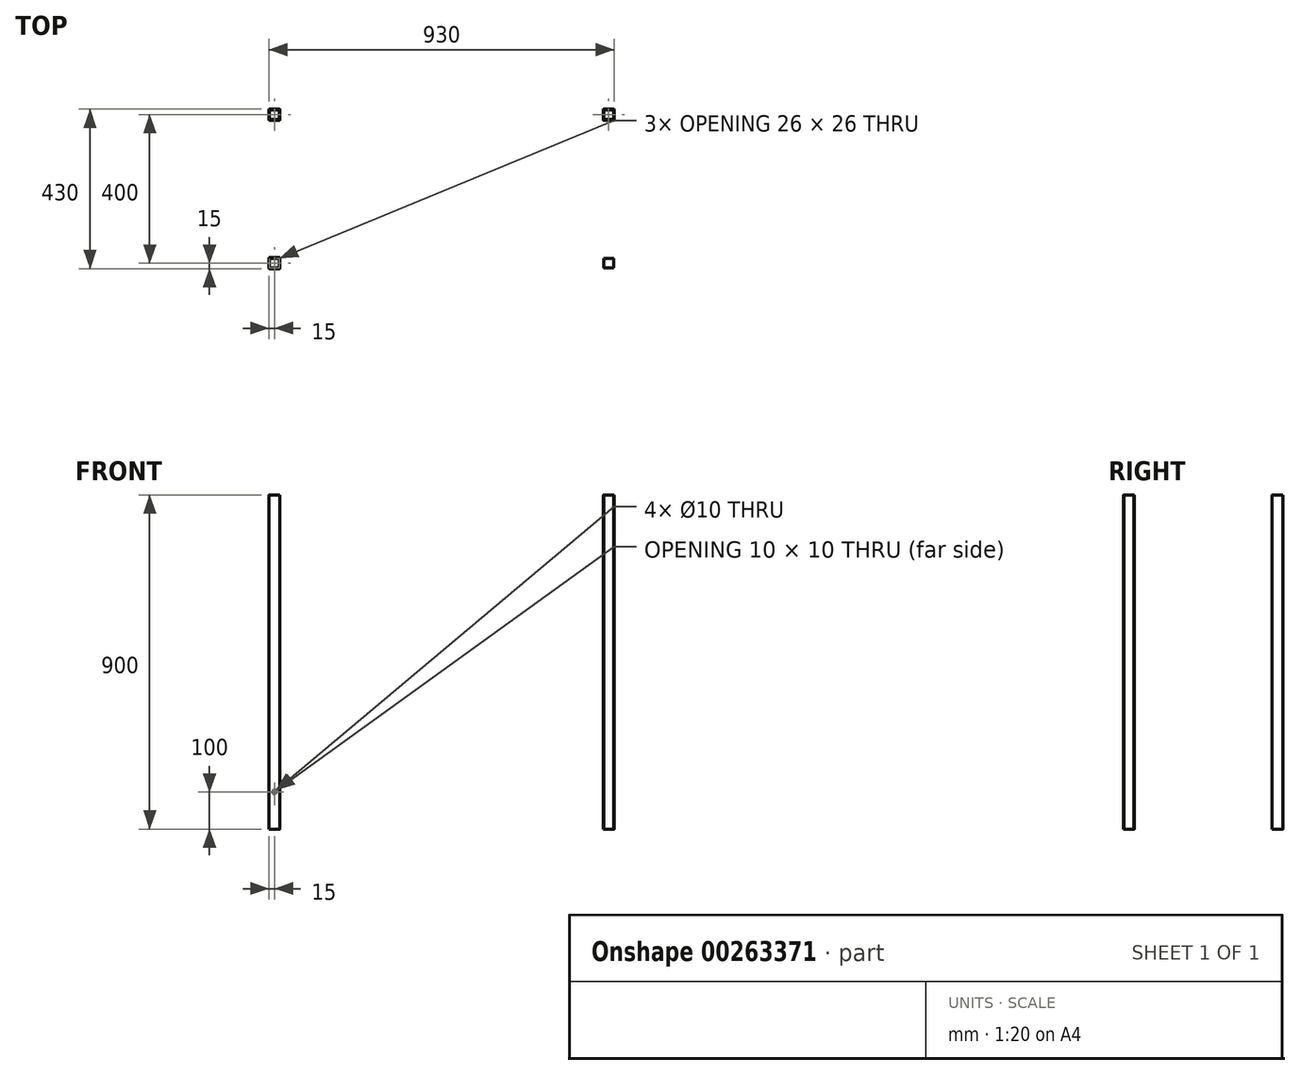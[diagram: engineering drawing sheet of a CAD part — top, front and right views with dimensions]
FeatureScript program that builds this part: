
annotation { "Feature Type Name" : "Feature", "Feature Type Description" : "" }
export const myFeature = defineFeature(function(context is Context, id is Id, definition is map)
    precondition{}
    {
        {
            var Q0;
            Q0=qCreatedBy(makeId("Top.planeOp"),FACE);
            var sketch = newSketch(context, id + "F0", { "sketchPlane" : qUnion([Q0])});
            skLineSegment(sketch, "E0.bottom", {"start": v(1, 0) * mm, "end": v(29, 0) * mm});
            skLineSegment(sketch, "E0.top", {"start": v(1, 30) * mm, "end": v(29, 30) * mm});
            skLineSegment(sketch, "E0.left", {"start": v(0, 1) * mm, "end": v(0, 29) * mm});
            skLineSegment(sketch, "E0.right", {"start": v(30, 1) * mm, "end": v(30, 29) * mm});
            skLineSegment(sketch, "E1.bottom", {"start": v(27, 28) * mm, "end": v(3, 28) * mm});
            skLineSegment(sketch, "E1.top", {"start": v(28, 2) * mm, "end": v(3, 2) * mm});
            skLineSegment(sketch, "E1.left", {"start": v(28, 27) * mm, "end": v(28, 2) * mm});
            skLineSegment(sketch, "E1.right", {"start": v(2, 27) * mm, "end": v(2, 3) * mm});
            skPoint(sketch, "E1.middle", {"position": v(15, 15) * mm});
            skLineSegment(sketch, "E2", {"start": v(15, 15) * mm, "end": v(15, 30) * mm, "construction": true});
            skLineSegment(sketch, "E3", {"start": v(15, 15) * mm, "end": v(0, 15) * mm, "construction": true});
            skPoint(sketch, "E4.visualSharp", {"position": v(0, 30) * mm});
            skArc(sketch, "E4.filletArc", {"start": v(1, 30) * mm, "mid": v(0.3, 29.7) * mm, "end": v(0, 29) * mm});
            skPoint(sketch, "E5.visualSharp", {"position": v(30, 30) * mm});
            skArc(sketch, "E5.filletArc", {"start": v(30, 29) * mm, "mid": v(29.7, 29.7) * mm, "end": v(29, 30) * mm});
            skPoint(sketch, "E6.visualSharp", {"position": v(30, 0) * mm});
            skArc(sketch, "E6.filletArc", {"start": v(29, 0) * mm, "mid": v(29.7, 0.3) * mm, "end": v(30, 1) * mm});
            skPoint(sketch, "E7.visualSharp", {"position": v(0, 0) * mm});
            skArc(sketch, "E7.filletArc", {"start": v(0, 1) * mm, "mid": v(0.3, 0.3) * mm, "end": v(1, 0) * mm});
            skPoint(sketch, "E8.visualSharp", {"position": v(2, 2) * mm});
            skArc(sketch, "E8.filletArc", {"start": v(2, 3) * mm, "mid": v(2.3, 2.3) * mm, "end": v(3, 2) * mm});
            skPoint(sketch, "E9.visualSharp", {"position": v(2, 28) * mm});
            skArc(sketch, "E9.filletArc", {"start": v(3, 28) * mm, "mid": v(2.3, 27.7) * mm, "end": v(2, 27) * mm});
            skPoint(sketch, "E10.visualSharp", {"position": v(28, 28) * mm});
            skArc(sketch, "E10.filletArc", {"start": v(28, 27) * mm, "mid": v(27.7, 27.7) * mm, "end": v(27, 28) * mm});
            skLineSegment(sketch, "E11.0.1.0", {"start": v(30, 401) * mm, "end": v(30, 429) * mm});
            skPoint(sketch, "E11.0.1.1", {"position": v(30, 430) * mm});
            skPoint(sketch, "E11.0.1.2", {"position": v(30, 400) * mm});
            skPoint(sketch, "E11.0.1.3", {"position": v(28, 428) * mm});
            skLineSegment(sketch, "E11.0.1.4", {"start": v(1, 400) * mm, "end": v(29, 400) * mm});
            skLineSegment(sketch, "E11.0.1.5", {"start": v(1, 430) * mm, "end": v(29, 430) * mm});
            skPoint(sketch, "E11.0.1.6", {"position": v(2, 428) * mm});
            skLineSegment(sketch, "E11.0.1.7", {"start": v(0, 401) * mm, "end": v(0, 429) * mm});
            skPoint(sketch, "E11.0.1.8", {"position": v(15, 415) * mm});
            skLineSegment(sketch, "E11.0.1.9", {"start": v(27, 428) * mm, "end": v(3, 428) * mm});
            skLineSegment(sketch, "E11.0.1.10", {"start": v(28, 427) * mm, "end": v(28, 402) * mm});
            skLineSegment(sketch, "E11.0.1.11", {"start": v(15, 415) * mm, "end": v(15, 430) * mm, "construction": true});
            skLineSegment(sketch, "E11.0.1.12", {"start": v(15, 415) * mm, "end": v(0, 415) * mm, "construction": true});
            skLineSegment(sketch, "E11.0.1.13", {"start": v(2, 427) * mm, "end": v(2, 403) * mm});
            skPoint(sketch, "E11.0.1.14", {"position": v(0, 400) * mm});
            skLineSegment(sketch, "E11.0.1.15", {"start": v(28, 402) * mm, "end": v(3, 402) * mm});
            skPoint(sketch, "E11.0.1.16", {"position": v(2, 402) * mm});
            skPoint(sketch, "E11.0.1.17", {"position": v(0, 430) * mm});
            skArc(sketch, "E11.0.1.18", {"start": v(1, 430) * mm, "mid": v(0.3, 429.7) * mm, "end": v(0, 429) * mm});
            skArc(sketch, "E11.0.1.19", {"start": v(30, 429) * mm, "mid": v(29.7, 429.7) * mm, "end": v(29, 430) * mm});
            skArc(sketch, "E11.0.1.20", {"start": v(28, 427) * mm, "mid": v(27.7, 427.7) * mm, "end": v(27, 428) * mm});
            skArc(sketch, "E11.0.1.21", {"start": v(0, 401) * mm, "mid": v(0.3, 400.3) * mm, "end": v(1, 400) * mm});
            skArc(sketch, "E11.0.1.22", {"start": v(2, 403) * mm, "mid": v(2.3, 402.3) * mm, "end": v(3, 402) * mm});
            skArc(sketch, "E11.0.1.23", {"start": v(3, 428) * mm, "mid": v(2.3, 427.7) * mm, "end": v(2, 427) * mm});
            skArc(sketch, "E11.0.1.24", {"start": v(29, 400) * mm, "mid": v(29.7, 400.3) * mm, "end": v(30, 401) * mm});
            skLineSegment(sketch, "E11.1.0.0", {"start": v(930, 1) * mm, "end": v(930, 29) * mm});
            skPoint(sketch, "E11.1.0.1", {"position": v(930, 30) * mm});
            skPoint(sketch, "E11.1.0.2", {"position": v(930, 0) * mm});
            skPoint(sketch, "E11.1.0.3", {"position": v(928, 28) * mm});
            skLineSegment(sketch, "E11.1.0.4", {"start": v(901, 0) * mm, "end": v(929, 0) * mm});
            skLineSegment(sketch, "E11.1.0.5", {"start": v(901, 30) * mm, "end": v(929, 30) * mm});
            skPoint(sketch, "E11.1.0.6", {"position": v(902, 28) * mm});
            skLineSegment(sketch, "E11.1.0.7", {"start": v(900, 1) * mm, "end": v(900, 29) * mm});
            skPoint(sketch, "E11.1.0.8", {"position": v(915, 15) * mm});
            skLineSegment(sketch, "E11.1.0.9", {"start": v(927, 28) * mm, "end": v(903, 28) * mm});
            skLineSegment(sketch, "E11.1.0.10", {"start": v(928, 27) * mm, "end": v(928, 2) * mm});
            skLineSegment(sketch, "E11.1.0.11", {"start": v(915, 15) * mm, "end": v(915, 30) * mm, "construction": true});
            skLineSegment(sketch, "E11.1.0.12", {"start": v(915, 15) * mm, "end": v(900, 15) * mm, "construction": true});
            skLineSegment(sketch, "E11.1.0.13", {"start": v(902, 27) * mm, "end": v(902, 3) * mm});
            skPoint(sketch, "E11.1.0.14", {"position": v(900, 0) * mm});
            skLineSegment(sketch, "E11.1.0.15", {"start": v(928, 2) * mm, "end": v(903, 2) * mm});
            skPoint(sketch, "E11.1.0.16", {"position": v(902, 2) * mm});
            skPoint(sketch, "E11.1.0.17", {"position": v(900, 30) * mm});
            skArc(sketch, "E11.1.0.18", {"start": v(901, 30) * mm, "mid": v(900.3, 29.7) * mm, "end": v(900, 29) * mm});
            skArc(sketch, "E11.1.0.19", {"start": v(930, 29) * mm, "mid": v(929.7, 29.7) * mm, "end": v(929, 30) * mm});
            skArc(sketch, "E11.1.0.20", {"start": v(928, 27) * mm, "mid": v(927.7, 27.7) * mm, "end": v(927, 28) * mm});
            skArc(sketch, "E11.1.0.21", {"start": v(900, 1) * mm, "mid": v(900.3, 0.3) * mm, "end": v(901, 0) * mm});
            skArc(sketch, "E11.1.0.22", {"start": v(902, 3) * mm, "mid": v(902.3, 2.3) * mm, "end": v(903, 2) * mm});
            skArc(sketch, "E11.1.0.23", {"start": v(903, 28) * mm, "mid": v(902.3, 27.7) * mm, "end": v(902, 27) * mm});
            skArc(sketch, "E11.1.0.24", {"start": v(929, 0) * mm, "mid": v(929.7, 0.3) * mm, "end": v(930, 1) * mm});
            skLineSegment(sketch, "E11.1.1.0", {"start": v(930, 401) * mm, "end": v(930, 429) * mm});
            skPoint(sketch, "E11.1.1.1", {"position": v(930, 430) * mm});
            skPoint(sketch, "E11.1.1.2", {"position": v(930, 400) * mm});
            skPoint(sketch, "E11.1.1.3", {"position": v(928, 428) * mm});
            skLineSegment(sketch, "E11.1.1.4", {"start": v(901, 400) * mm, "end": v(929, 400) * mm});
            skLineSegment(sketch, "E11.1.1.5", {"start": v(901, 430) * mm, "end": v(929, 430) * mm});
            skPoint(sketch, "E11.1.1.6", {"position": v(902, 428) * mm});
            skLineSegment(sketch, "E11.1.1.7", {"start": v(900, 401) * mm, "end": v(900, 429) * mm});
            skPoint(sketch, "E11.1.1.8", {"position": v(915, 415) * mm});
            skLineSegment(sketch, "E11.1.1.9", {"start": v(927, 428) * mm, "end": v(903, 428) * mm});
            skLineSegment(sketch, "E11.1.1.10", {"start": v(928, 427) * mm, "end": v(928, 402) * mm});
            skLineSegment(sketch, "E11.1.1.11", {"start": v(915, 415) * mm, "end": v(915, 430) * mm, "construction": true});
            skLineSegment(sketch, "E11.1.1.12", {"start": v(915, 415) * mm, "end": v(900, 415) * mm, "construction": true});
            skLineSegment(sketch, "E11.1.1.13", {"start": v(902, 427) * mm, "end": v(902, 403) * mm});
            skPoint(sketch, "E11.1.1.14", {"position": v(900, 400) * mm});
            skLineSegment(sketch, "E11.1.1.15", {"start": v(928, 402) * mm, "end": v(903, 402) * mm});
            skPoint(sketch, "E11.1.1.16", {"position": v(902, 402) * mm});
            skPoint(sketch, "E11.1.1.17", {"position": v(900, 430) * mm});
            skArc(sketch, "E11.1.1.18", {"start": v(901, 430) * mm, "mid": v(900.3, 429.7) * mm, "end": v(900, 429) * mm});
            skArc(sketch, "E11.1.1.19", {"start": v(930, 429) * mm, "mid": v(929.7, 429.7) * mm, "end": v(929, 430) * mm});
            skArc(sketch, "E11.1.1.20", {"start": v(928, 427) * mm, "mid": v(927.7, 427.7) * mm, "end": v(927, 428) * mm});
            skArc(sketch, "E11.1.1.21", {"start": v(900, 401) * mm, "mid": v(900.3, 400.3) * mm, "end": v(901, 400) * mm});
            skArc(sketch, "E11.1.1.22", {"start": v(902, 403) * mm, "mid": v(902.3, 402.3) * mm, "end": v(903, 402) * mm});
            skArc(sketch, "E11.1.1.23", {"start": v(903, 428) * mm, "mid": v(902.3, 427.7) * mm, "end": v(902, 427) * mm});
            skArc(sketch, "E11.1.1.24", {"start": v(929, 400) * mm, "mid": v(929.7, 400.3) * mm, "end": v(930, 401) * mm});
            skLineSegment(sketch, "E11.direction1", {"start": v(0, 0) * mm, "end": v(900, 0) * mm, "construction": true});
            skLineSegment(sketch, "E11.direction2", {"start": v(0, 0) * mm, "end": v(0, 400) * mm, "construction": true});
            skSolve(sketch);
        }
        {
            var Q0;
            Q0=sQuery(id+"F0.wireOp",EDGE,"E0.top");
            var Q1;
            Q1=sQuery(id+"F0.wireOp",EDGE,"E1.bottom");
            var Q2;
            Q2=sQuery(id+"F0.wireOp",EDGE,"E1.left");
            var Q3;
            Q3=sQuery(id+"F0.wireOp",EDGE,"E0.right");
            var Q4;
            Q4=sQuery(id+"F0.wireOp",EDGE,"E0.left");
            var Q5;
            Q5=sQuery(id+"F0.wireOp",EDGE,"E1.right");
            var Q6;
            Q6=sQuery(id+"F0.wireOp",EDGE,"E1.top");
            var Q7;
            Q7=sQuery(id+"F0.wireOp",EDGE,"E0.bottom");
            extrude(context, id + "F1", {"bodyType" : ToolBodyType.SURFACE, "surfaceEntities" : qUnion([Q0, Q1, Q2, Q3, Q4, Q5, Q6, Q7]), "depth" : 900 * mm});
        }
        {
            var Q0;
            Q0=makeQuery(id+"F0.imprint","IMPRINT",FACE,{"disambiguationData":[TD([[makeQuery(id+"F0.imprint","IMPRINT",EDGE,{"derivedFrom":sQuery(id+"F0.wireOp",EDGE,"E0.bottom")}),1.0]])]});
            var Q1;
            Q1=makeQuery(id+"F0.imprint","IMPRINT",FACE,{"disambiguationData":[TD([[makeQuery(id+"F0.imprint","IMPRINT",EDGE,{"derivedFrom":sQuery(id+"F0.wireOp",EDGE,"E11.0.1.0")}),1.0]])]});
            var Q2;
            Q2=makeQuery(id+"F0.imprint","IMPRINT",FACE,{"disambiguationData":[TD([[makeQuery(id+"F0.imprint","IMPRINT",EDGE,{"derivedFrom":sQuery(id+"F0.wireOp",EDGE,"E11.1.0.9")}),1.0]])]});
            var Q3;
            Q3=makeQuery(id+"F0.imprint","IMPRINT",FACE,{"disambiguationData":[TD([[makeQuery(id+"F0.imprint","IMPRINT",EDGE,{"derivedFrom":sQuery(id+"F0.wireOp",EDGE,"E11.1.1.0")}),1.0]])]});
            extrude(context, id + "F2", {"entities" : qUnion([Q0, Q1, Q2, Q3]), "depth" : 900 * mm});
        }
        {
            var Q0;
            Q0=makeQuery(id+"F1.opExtrude","SWEPT_FACE",FACE,{"disambiguationData":[OSD([sQuery(id+"F0.wireOp",EDGE,"E0.bottom")])]});
            var sketch = newSketch(context, id + "F3", { "sketchPlane" : qUnion([Q0])});
            skCircle(sketch, "E12", {"center": v(15, 100) * mm, "radius": 5 * mm});
            skSolve(sketch);
        }
        {
            var Q0;
            Q0=makeQuery(id+"F3.imprint","IMPRINT",FACE,{"disambiguationData":[TD([[makeQuery(id+"F3.imprint","IMPRINT",EDGE,{"derivedFrom":sQuery(id+"F3.wireOp",EDGE,"E12")}),1.0]])]});
            extrude(context, id + "F4", {"entities" : qUnion([Q0]), "operationType" : NewBodyOperationType.REMOVE, "oppositeDirection" : true, "depth" : 30 * mm});
        }
        {
            var Q0;
            Q0=makeQuery(id+"F2.opExtrude","SWEPT_FACE",FACE,{"disambiguationData":[OSD([sQuery(id+"F0.wireOp",EDGE,"E11.0.1.5")])]});
            var sketch = newSketch(context, id + "F5", { "sketchPlane" : qUnion([Q0])});
            skLineSegment(sketch, "E13", {"start": v(-29, 100) * mm, "end": v(-1, 100) * mm, "construction": true});
            skCircle(sketch, "E14", {"center": v(-15, 100) * mm, "radius": 5 * mm});
            skPoint(sketch, "E15", {"position": v(-15, 0) * mm});
            skSolve(sketch);
        }
        {
            var Q0;
            Q0=makeQuery(id+"F5.imprint","IMPRINT",FACE,{"disambiguationData":[TD([[makeQuery(id+"F5.imprint","IMPRINT",EDGE,{"derivedFrom":sQuery(id+"F5.wireOp",EDGE,"E14")}),1.0]])]});
            extrude(context, id + "F6", {"entities" : qUnion([Q0]), "operationType" : NewBodyOperationType.REMOVE, "oppositeDirection" : true, "depth" : 30 * mm});
        }
        {
            var Q0;
            Q0=makeQuery(id+"F0.imprint","IMPRINT",FACE,{"disambiguationData":[TD([[makeQuery(id+"F0.imprint","IMPRINT",EDGE,{"derivedFrom":sQuery(id+"F0.wireOp",EDGE,"E1.bottom")}),1.0]])]});
            extrude(context, id + "F7", {"entities" : qUnion([Q0]), "operationType" : NewBodyOperationType.REMOVE, "oppositeDirection" : true, "depth" : 25 * mm});
        }
    });
